AUTODESK INVENTOR PART (.ipt)
format: ipt  version: 2021 (Build 250183000, 183)  size: 403,456 bytes
history: native  units: mm
features: extrude x9, sketch x9, other x1, plane x1
ambient origin geometry x8: Origin, YZ Plane, XZ Plane, XY Plane, X Axis, Y Axis, Z Axis, Center Point
bodies: Volumenkörper1 (feature_tree)
feature tree (20):
  other  "Zahnrad_außen"
  extrude  "Extrusion1"  Depth=12.0mm
  extrude  "Extrusion3"  Depth=6.0mm TaperAngle=0.0deg
  extrude  "Extrusion9"  Depth=12.0mm
  extrude  "Extrusion10"  Depth=12.0mm TaperAngle=0.0deg
  extrude  "Extrusion12"  Depth=4.0mm TaperAngle=0.0deg
  extrude  "Extrusion13"  Depth=2.0mm
  extrude  "Extrusion14"  Depth=2.0mm
  extrude  "Extrusion15"  Depth=2.0mm
  plane  "Arbeitsebene2"
  extrude  "Extrusion16"  Depth=2.0mm
  sketch  "Skizze1"  dims[d10=12.0mm d12=17.0mm]
  sketch  "Skizze3"  dims[d21=6.0mm d22=0.0mm d33=6.0mm d34=0.0mm]
  sketch  "Skizze9"  dims[d53=12.0mm d54=12.0mm]
  sketch  "Skizze10"  dims[d55=12.0mm d56=6.0mm d57=0.0mm]
  sketch  "Skizze12"  dims[d58=7.5mm d59=4.0mm d60=0.0mm]
  sketch  "Skizze13"  dims[d64=2.0mm d65=2.0mm]
  sketch  "Skizze14"  dims[d66=2.0mm d67=2.0mm]
  sketch  "Skizze15"  dims[d68=2.0mm d69=2.0mm]
  sketch  "Skizze17"  dims[d70=2.0mm d71=2.0mm d72=4.0mm d73=0.0mm d76=3.0mm d77=3.0mm d78=3.0mm d79=3.0mm d80=3.0mm d81=3.0mm d82=3.0mm d83=3.0mm d84=90.0deg d85=2.5mm d86=2.5mm d87=2.5mm d88=2.5mm d89=90.0deg d90=17.0mm d91=2.0mm d92=0.0mm d93=3.2mm d94=2.0mm d95=0.0mm d96=18.0mm d97=3.0mm d98=0.0mm d99=17.0mm d101=-1.5mm d102=18.5mm d103=2.0mm d104=0.0mm]
